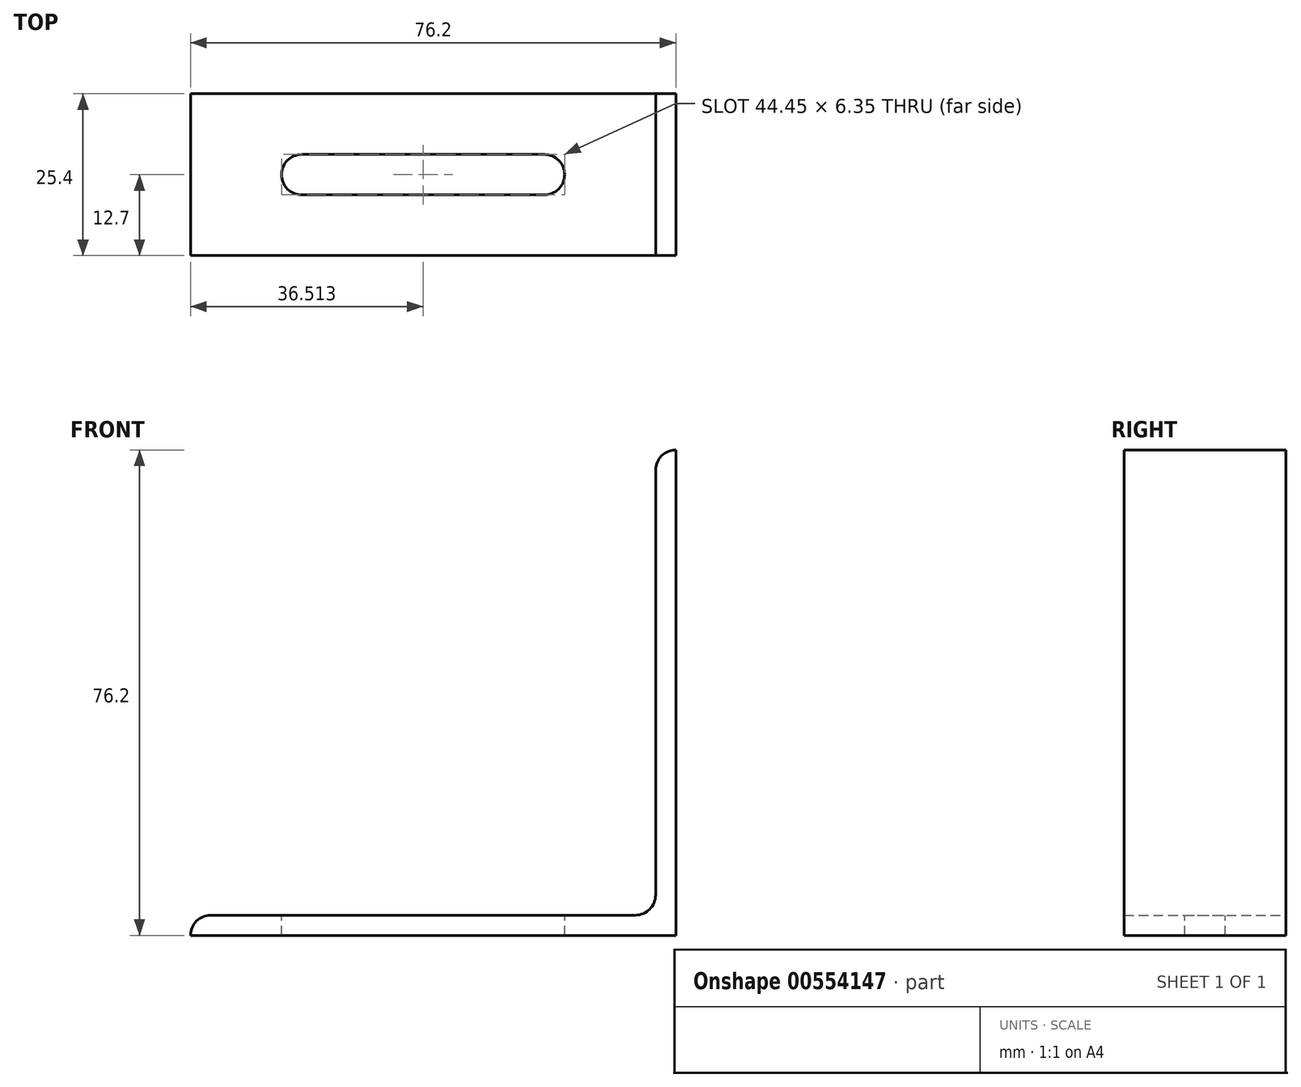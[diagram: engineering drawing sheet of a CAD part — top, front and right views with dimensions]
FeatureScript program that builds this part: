
annotation { "Feature Type Name" : "Feature", "Feature Type Description" : "" }
export const myFeature = defineFeature(function(context is Context, id is Id, definition is map)
    precondition{}
    {
        {
            var Q0;
            Q0=qCreatedBy(makeId("Front.planeOp"),FACE);
            var sketch = newSketch(context, id + "F0", { "sketchPlane" : qUnion([Q0])});
            skLineSegment(sketch, "E0", {"start": v(0, 0) * mm, "end": v(76.2, 0) * mm});
            skLineSegment(sketch, "E1", {"start": v(76.2, 0) * mm, "end": v(76.2, 76.2) * mm});
            skLineSegment(sketch, "E2", {"start": v(76.2, 76.2) * mm, "end": v(76.2, 76.2) * mm});
            skLineSegment(sketch, "E3", {"start": v(73.03, 73.03) * mm, "end": v(73.03, 6.35) * mm});
            skLineSegment(sketch, "E4", {"start": v(69.85, 3.18) * mm, "end": v(3.18, 3.18) * mm});
            skLineSegment(sketch, "E5", {"start": v(0, 0) * mm, "end": v(0, 0) * mm});
            skPoint(sketch, "E6.visualSharp", {"position": v(73.03, 3.18) * mm});
            skArc(sketch, "E6.filletArc", {"start": v(69.85, 3.18) * mm, "mid": v(72.1, 4.1) * mm, "end": v(73.03, 6.35) * mm});
            skPoint(sketch, "E7.visualSharp", {"position": v(73.03, 76.2) * mm});
            skArc(sketch, "E7.filletArc", {"start": v(76.2, 76.2) * mm, "mid": v(73.95, 75.27) * mm, "end": v(73.02, 73.03) * mm});
            skPoint(sketch, "E8.visualSharp", {"position": v(0, 3.18) * mm});
            skArc(sketch, "E8.filletArc", {"start": v(3.18, 3.18) * mm, "mid": v(0.93, 2.25) * mm, "end": v(0, 0) * mm});
            skSolve(sketch);
        }
        {
            var Q0;
            Q0=makeQuery(id+"F0.imprint","IMPRINT",FACE,{"disambiguationData":[TD([[makeQuery(id+"F0.imprint","IMPRINT",EDGE,{"derivedFrom":sQuery(id+"F0.wireOp",EDGE,"E0")}),1.0]])]});
            extrude(context, id + "F1", {"entities" : qUnion([Q0]), "depth" : 25.4 * mm, "offsetDistance" : 25.4 * mm});
        }
        {
            var Q0;
            Q0=makeQuery(id+"F1.opExtrude","SWEPT_FACE",FACE,{"disambiguationData":[OSD([sQuery(id+"F0.wireOp",EDGE,"E4")])]});
            var sketch = newSketch(context, id + "F2", { "sketchPlane" : qUnion([Q0])});
            skArc(sketch, "E9", {"start": v(17.46, -9.53) * mm, "mid": v(14.29, -12.7) * mm, "end": v(17.46, -15.88) * mm});
            skArc(sketch, "E10", {"start": v(55.56, -15.88) * mm, "mid": v(58.74, -12.7) * mm, "end": v(55.56, -9.53) * mm});
            skLineSegment(sketch, "E11", {"start": v(55.56, -9.53) * mm, "end": v(17.46, -9.53) * mm});
            skLineSegment(sketch, "E12", {"start": v(17.46, -15.88) * mm, "end": v(55.56, -15.88) * mm});
            skSolve(sketch);
        }
        {
            var Q0;
            Q0=makeQuery(id+"F2.imprint","IMPRINT",FACE,{"disambiguationData":[TD([[makeQuery(id+"F2.imprint","IMPRINT",EDGE,{"derivedFrom":sQuery(id+"F2.wireOp",EDGE,"E9")}),1.0]])]});
            extrude(context, id + "F3", {"entities" : qUnion([Q0]), "operationType" : NewBodyOperationType.REMOVE, "endBound" : BoundingType.THROUGH_ALL, "oppositeDirection" : true, "depth" : 25.4 * mm, "offsetDistance" : 25.4 * mm});
        }
    });
